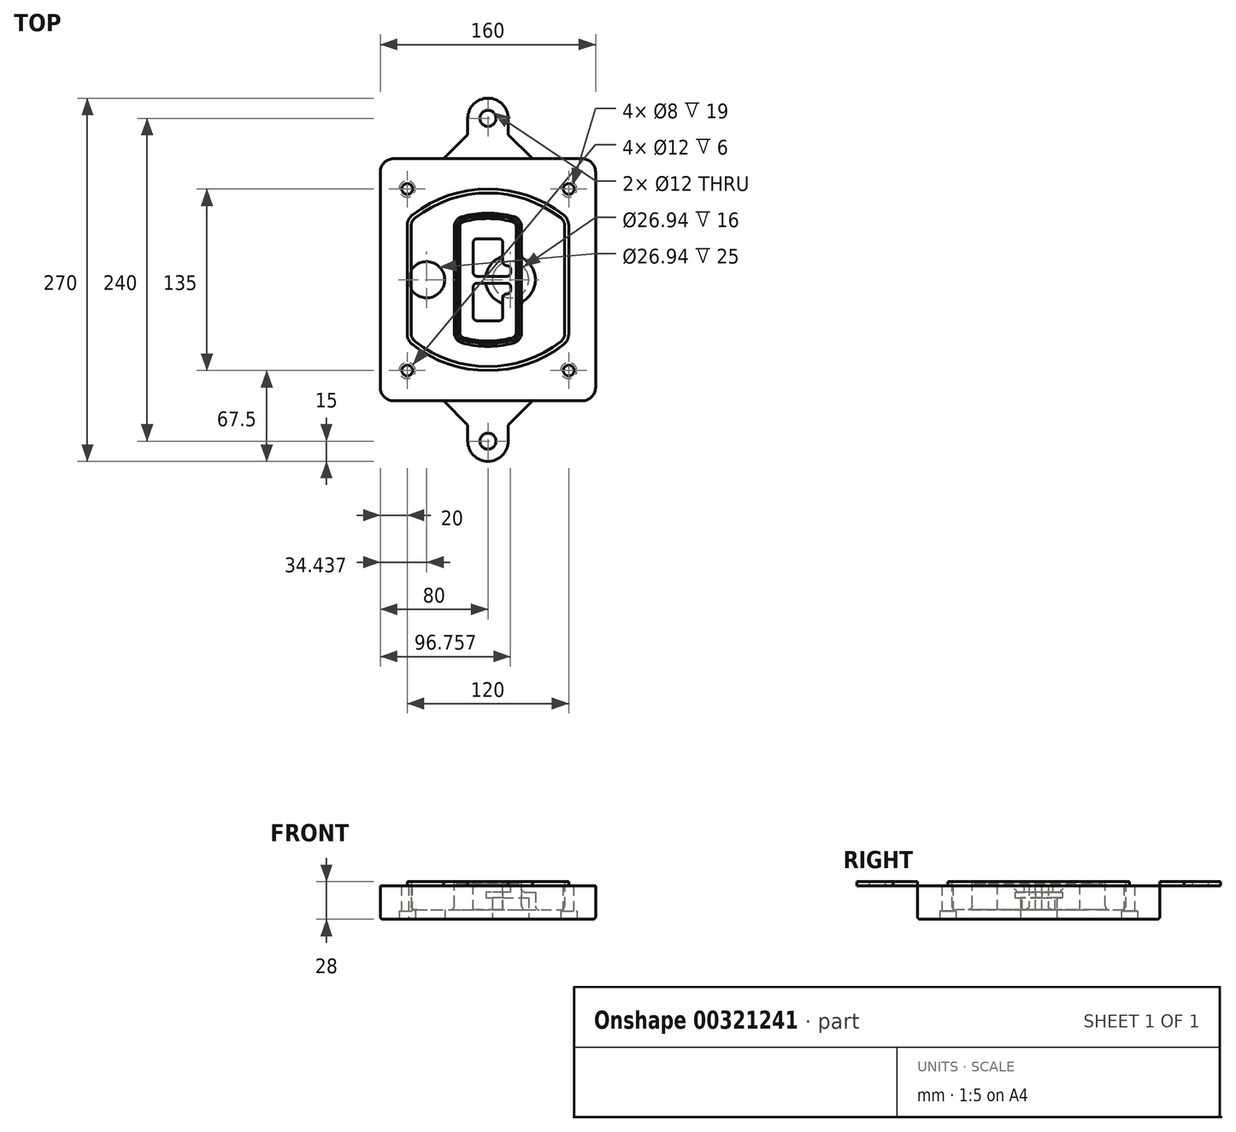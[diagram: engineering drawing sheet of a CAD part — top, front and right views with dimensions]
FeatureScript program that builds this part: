
annotation { "Feature Type Name" : "Feature", "Feature Type Description" : "" }
export const myFeature = defineFeature(function(context is Context, id is Id, definition is map)
    precondition{}
    {
        {
            var Q0;
            Q0=qCreatedBy(makeId("Top.planeOp"),FACE);
            var sketch = newSketch(context, id + "F0", { "sketchPlane" : qUnion([Q0])});
            skPoint(sketch, "E0.rect.middle", {"position": v(0, 0) * mm});
            skLineSegment(sketch, "E1.bottom", {"start": v(-70, -90) * mm, "end": v(70, -90) * mm});
            skLineSegment(sketch, "E1.top", {"start": v(-70, 90) * mm, "end": v(70, 90) * mm});
            skLineSegment(sketch, "E1.left", {"start": v(-80, -80) * mm, "end": v(-80, 80) * mm});
            skLineSegment(sketch, "E1.right", {"start": v(80, -80) * mm, "end": v(80, 80) * mm});
            skLineSegment(sketch, "E2", {"start": v(-80, 90) * mm, "end": v(80, -90) * mm, "construction": true});
            skLineSegment(sketch, "E3", {"start": v(80, 90) * mm, "end": v(-80, -90) * mm, "construction": true});
            skCircle(sketch, "E4", {"center": v(-60, 67.5) * mm, "radius": 4 * mm});
            skCircle(sketch, "E5", {"center": v(60, 67.5) * mm, "radius": 4 * mm});
            skCircle(sketch, "E6", {"center": v(60, -67.5) * mm, "radius": 4 * mm});
            skCircle(sketch, "E7", {"center": v(-60, -67.5) * mm, "radius": 4 * mm});
            skLineSegment(sketch, "E8", {"start": v(-60, 67.5) * mm, "end": v(60, 67.5) * mm, "construction": true});
            skLineSegment(sketch, "E9", {"start": v(60, 67.5) * mm, "end": v(60, -67.5) * mm, "construction": true});
            skLineSegment(sketch, "E10", {"start": v(60, -67.5) * mm, "end": v(-60, -67.5) * mm, "construction": true});
            skLineSegment(sketch, "E11", {"start": v(-60, -67.5) * mm, "end": v(-60, 67.5) * mm, "construction": true});
            skLineSegment(sketch, "E12", {"start": v(-60, 40.3) * mm, "end": v(-60, -40.3) * mm});
            skLineSegment(sketch, "E13", {"start": v(60, 40.3) * mm, "end": v(60, -40.3) * mm});
            skArc(sketch, "E14", {"start": v(56.15, 48.18) * mm, "mid": v(0, 67.5) * mm, "end": v(-56.15, 48.18) * mm});
            skArc(sketch, "E15", {"start": v(-56.15, -48.18) * mm, "mid": v(0, -67.5) * mm, "end": v(56.15, -48.18) * mm});
            skLineSegment(sketch, "E16", {"start": v(-60, 0) * mm, "end": v(60, 0) * mm, "construction": true});
            skPoint(sketch, "E17.visualSharp", {"position": v(-60, -45) * mm});
            skArc(sketch, "E17.filletArc", {"start": v(-60, -40.3) * mm, "mid": v(-58.99, -44.68) * mm, "end": v(-56.15, -48.18) * mm});
            skPoint(sketch, "E18.visualSharp", {"position": v(-60, 45) * mm});
            skArc(sketch, "E18.filletArc", {"start": v(-56.15, 48.18) * mm, "mid": v(-58.99, 44.68) * mm, "end": v(-60, 40.3) * mm});
            skPoint(sketch, "E19.visualSharp", {"position": v(60, 45) * mm});
            skArc(sketch, "E19.filletArc", {"start": v(60, 40.3) * mm, "mid": v(58.99, 44.68) * mm, "end": v(56.15, 48.18) * mm});
            skPoint(sketch, "E20.visualSharp", {"position": v(60, -45) * mm});
            skArc(sketch, "E20.filletArc", {"start": v(56.15, -48.18) * mm, "mid": v(58.99, -44.68) * mm, "end": v(60, -40.3) * mm});
            skPoint(sketch, "E21.visualSharp", {"position": v(-80, 90) * mm});
            skArc(sketch, "E21.filletArc", {"start": v(-70, 90) * mm, "mid": v(-77.07, 87.07) * mm, "end": v(-80, 80) * mm});
            skPoint(sketch, "E22.visualSharp", {"position": v(80, 90) * mm});
            skArc(sketch, "E22.filletArc", {"start": v(80, 80) * mm, "mid": v(77.07, 87.07) * mm, "end": v(70, 90) * mm});
            skPoint(sketch, "E23.visualSharp", {"position": v(80, -90) * mm});
            skArc(sketch, "E23.filletArc", {"start": v(70, -90) * mm, "mid": v(77.07, -87.07) * mm, "end": v(80, -80) * mm});
            skPoint(sketch, "E24.visualSharp", {"position": v(-80, -90) * mm});
            skArc(sketch, "E24.filletArc", {"start": v(-80, -80) * mm, "mid": v(-77.07, -87.07) * mm, "end": v(-70, -90) * mm});
            skArc(sketch, "E25.0", {"start": v(57, 40.3) * mm, "mid": v(56.3, 43.36) * mm, "end": v(54.3, 45.81) * mm});
            skLineSegment(sketch, "E25.1", {"start": v(57, 40.3) * mm, "end": v(57, -40.3) * mm});
            skArc(sketch, "E25.2", {"start": v(54.3, -45.81) * mm, "mid": v(56.3, -43.36) * mm, "end": v(57, -40.3) * mm});
            skArc(sketch, "E25.3", {"start": v(-54.3, -45.81) * mm, "mid": v(0, -64.5) * mm, "end": v(54.3, -45.81) * mm});
            skArc(sketch, "E25.4", {"start": v(-57, -40.3) * mm, "mid": v(-56.3, -43.36) * mm, "end": v(-54.3, -45.81) * mm});
            skArc(sketch, "E25.5", {"start": v(54.3, 45.81) * mm, "mid": v(0, 64.5) * mm, "end": v(-54.3, 45.81) * mm});
            skLineSegment(sketch, "E25.6", {"start": v(-57, 40.3) * mm, "end": v(-57, -40.3) * mm});
            skArc(sketch, "E25.7", {"start": v(-54.3, 45.81) * mm, "mid": v(-56.3, 43.36) * mm, "end": v(-57, 40.3) * mm});
            skArc(sketch, "E26.0", {"start": v(-58.62, 51.33) * mm, "mid": v(-62.58, 46.43) * mm, "end": v(-64, 40.3) * mm});
            skArc(sketch, "E26.1", {"start": v(58.62, 51.33) * mm, "mid": v(0, 71.5) * mm, "end": v(-58.62, 51.33) * mm});
            skArc(sketch, "E26.2", {"start": v(64, 40.3) * mm, "mid": v(62.58, 46.43) * mm, "end": v(58.62, 51.33) * mm});
            skLineSegment(sketch, "E26.3", {"start": v(64, 40.3) * mm, "end": v(64, -40.3) * mm});
            skArc(sketch, "E26.4", {"start": v(58.62, -51.33) * mm, "mid": v(62.58, -46.43) * mm, "end": v(64, -40.3) * mm});
            skLineSegment(sketch, "E26.5", {"start": v(-64, 40.3) * mm, "end": v(-64, -40.3) * mm});
            skArc(sketch, "E26.6", {"start": v(-58.62, -51.33) * mm, "mid": v(0, -71.5) * mm, "end": v(58.62, -51.33) * mm});
            skArc(sketch, "E26.7", {"start": v(-64, -40.3) * mm, "mid": v(-62.58, -46.43) * mm, "end": v(-58.62, -51.33) * mm});
            skSolve(sketch);
        }
        {
            var Q0;
            Q0=makeQuery(id+"F0.imprint","IMPRINT",FACE,{"disambiguationData":[TD([[makeQuery(id+"F0.imprint","IMPRINT",EDGE,{"derivedFrom":sQuery(id+"F0.wireOp",EDGE,"E1.bottom")}),1.0]])]});
            var Q1;
            Q1=makeQuery(id+"F0.imprint","IMPRINT",FACE,{"disambiguationData":[TD([[makeQuery(id+"F0.imprint","IMPRINT",EDGE,{"derivedFrom":sQuery(id+"F0.wireOp",EDGE,"E12")}),1.0]])]});
            var Q2;
            Q2=makeQuery(id+"F0.imprint","IMPRINT",FACE,{"disambiguationData":[TD([[makeQuery(id+"F0.imprint","IMPRINT",EDGE,{"derivedFrom":sQuery(id+"F0.wireOp",EDGE,"E25.0")}),1.0]])]});
            var Q3;
            Q3=makeQuery(id+"F0.imprint","IMPRINT",FACE,{"disambiguationData":[TD([[makeQuery(id+"F0.imprint","IMPRINT",EDGE,{"derivedFrom":sQuery(id+"F0.wireOp",EDGE,"E12")}),-1.0]])]});
            extrude(context, id + "F1", {"entities" : qUnion([Q0, Q1, Q2, Q3]), "oppositeDirection" : true, "depth" : 25 * mm});
        }
        {
            var Q0;
            Q0=makeQuery(id+"F0.imprint","IMPRINT",FACE,{"disambiguationData":[TD([[makeQuery(id+"F0.imprint","IMPRINT",EDGE,{"derivedFrom":sQuery(id+"F0.wireOp",EDGE,"E12")}),1.0]])]});
            extrude(context, id + "F2", {"entities" : qUnion([Q0]), "operationType" : NewBodyOperationType.ADD, "depth" : 3 * mm});
        }
        {
            var Q0;
            Q0=makeQuery(id+"F0.imprint","IMPRINT",FACE,{"disambiguationData":[TD([[makeQuery(id+"F0.imprint","IMPRINT",EDGE,{"derivedFrom":sQuery(id+"F0.wireOp",EDGE,"E25.0")}),1.0]])]});
            extrude(context, id + "F3", {"entities" : qUnion([Q0]), "operationType" : NewBodyOperationType.REMOVE, "oppositeDirection" : true, "depth" : 18 * mm});
        }
        {
            var Q0;
            Q0=makeQuery(id+"F2.opExtrude","CAP_FACE",FACE,{"disambiguationData":[OSD([sQuery(id+"F0.wireOp",EDGE,"E12"),sQuery(id+"F0.wireOp",EDGE,"E13"),sQuery(id+"F0.wireOp",EDGE,"E14"),sQuery(id+"F0.wireOp",EDGE,"E15"),sQuery(id+"F0.wireOp",EDGE,"E17.filletArc"),sQuery(id+"F0.wireOp",EDGE,"E18.filletArc"),sQuery(id+"F0.wireOp",EDGE,"E19.filletArc"),sQuery(id+"F0.wireOp",EDGE,"E20.filletArc"),sQuery(id+"F0.wireOp",EDGE,"E25.0"),sQuery(id+"F0.wireOp",EDGE,"E25.1"),sQuery(id+"F0.wireOp",EDGE,"E25.2"),sQuery(id+"F0.wireOp",EDGE,"E25.3"),sQuery(id+"F0.wireOp",EDGE,"E25.4"),sQuery(id+"F0.wireOp",EDGE,"E25.5"),sQuery(id+"F0.wireOp",EDGE,"E25.6"),sQuery(id+"F0.wireOp",EDGE,"E25.7")])],"isStart":false});
            var sketch = newSketch(context, id + "F4", { "sketchPlane" : qUnion([Q0])});
            skArc(sketch, "E27.0", {"start": v(-19.08, -46.97) * mm, "mid": v(0, -49.5) * mm, "end": v(19.08, -46.97) * mm});
            skArc(sketch, "E28.0", {"start": v(19.08, 46.97) * mm, "mid": v(0, 49.5) * mm, "end": v(-19.08, 46.97) * mm});
            skLineSegment(sketch, "E29", {"start": v(-25, 39.25) * mm, "end": v(-25, -39.25) * mm});
            skLineSegment(sketch, "E30", {"start": v(25, 39.25) * mm, "end": v(25, -39.25) * mm});
            skLineSegment(sketch, "E31", {"start": v(-25, 45.1) * mm, "end": v(25, 45.1) * mm, "construction": true});
            skLineSegment(sketch, "E32", {"start": v(-25, -45.1) * mm, "end": v(25, -45.1) * mm, "construction": true});
            skPoint(sketch, "E33.visualSharp", {"position": v(-25, 45.1) * mm});
            skArc(sketch, "E33.filletArc", {"start": v(-19.08, 46.97) * mm, "mid": v(-23.35, 44.11) * mm, "end": v(-25, 39.25) * mm});
            skPoint(sketch, "E34.visualSharp", {"position": v(25, 45.1) * mm});
            skArc(sketch, "E34.filletArc", {"start": v(25, 39.25) * mm, "mid": v(23.35, 44.11) * mm, "end": v(19.08, 46.97) * mm});
            skPoint(sketch, "E35.visualSharp", {"position": v(25, -45.1) * mm});
            skArc(sketch, "E35.filletArc", {"start": v(19.08, -46.97) * mm, "mid": v(23.35, -44.11) * mm, "end": v(25, -39.25) * mm});
            skPoint(sketch, "E36.visualSharp", {"position": v(-25, -45.1) * mm});
            skArc(sketch, "E36.filletArc", {"start": v(-25, -39.25) * mm, "mid": v(-23.35, -44.11) * mm, "end": v(-19.08, -46.97) * mm});
            skArc(sketch, "E37.0", {"start": v(54.3, 45.81) * mm, "mid": v(0, 64.5) * mm, "end": v(-54.3, 45.81) * mm});
            skArc(sketch, "E37.1", {"start": v(-54.3, 45.81) * mm, "mid": v(-56.3, 43.36) * mm, "end": v(-57, 40.3) * mm});
            skLineSegment(sketch, "E37.2", {"start": v(-57, 40.3) * mm, "end": v(-57, -40.3) * mm});
            skArc(sketch, "E37.3", {"start": v(-57, -40.3) * mm, "mid": v(-56.3, -43.36) * mm, "end": v(-54.3, -45.81) * mm});
            skArc(sketch, "E37.4", {"start": v(-54.3, -45.81) * mm, "mid": v(0, -64.5) * mm, "end": v(54.3, -45.81) * mm});
            skArc(sketch, "E37.5", {"start": v(54.3, -45.81) * mm, "mid": v(56.3, -43.36) * mm, "end": v(57, -40.3) * mm});
            skLineSegment(sketch, "E37.6", {"start": v(57, 40.3) * mm, "end": v(57, -40.3) * mm});
            skArc(sketch, "E37.7", {"start": v(57, 40.3) * mm, "mid": v(56.3, 43.36) * mm, "end": v(54.3, 45.81) * mm});
            skLineSegment(sketch, "E38.0", {"start": v(23, 39.25) * mm, "end": v(23, -39.25) * mm});
            skArc(sketch, "E38.1", {"start": v(18.56, -45.04) * mm, "mid": v(21.76, -42.9) * mm, "end": v(23, -39.25) * mm});
            skArc(sketch, "E38.2", {"start": v(-18.56, -45.04) * mm, "mid": v(0, -47.5) * mm, "end": v(18.56, -45.04) * mm});
            skArc(sketch, "E38.3", {"start": v(-23, -39.25) * mm, "mid": v(-21.76, -42.9) * mm, "end": v(-18.56, -45.04) * mm});
            skLineSegment(sketch, "E38.4", {"start": v(-23, 39.25) * mm, "end": v(-23, -39.25) * mm});
            skArc(sketch, "E38.5", {"start": v(23, 39.25) * mm, "mid": v(21.76, 42.9) * mm, "end": v(18.56, 45.04) * mm});
            skArc(sketch, "E38.6", {"start": v(-18.56, 45.04) * mm, "mid": v(-21.76, 42.9) * mm, "end": v(-23, 39.25) * mm});
            skArc(sketch, "E38.7", {"start": v(18.56, 45.04) * mm, "mid": v(0, 47.5) * mm, "end": v(-18.56, 45.04) * mm});
            skArc(sketch, "E39.0", {"start": v(21, 39.25) * mm, "mid": v(20.18, 41.68) * mm, "end": v(18.04, 43.1) * mm});
            skLineSegment(sketch, "E39.1", {"start": v(21, 39.25) * mm, "end": v(21, -39.25) * mm});
            skArc(sketch, "E39.2", {"start": v(18.04, -43.1) * mm, "mid": v(20.18, -41.68) * mm, "end": v(21, -39.25) * mm});
            skArc(sketch, "E39.3", {"start": v(-18.04, -43.1) * mm, "mid": v(0, -45.5) * mm, "end": v(18.04, -43.1) * mm});
            skArc(sketch, "E39.4", {"start": v(-21, -39.25) * mm, "mid": v(-20.18, -41.68) * mm, "end": v(-18.04, -43.1) * mm});
            skArc(sketch, "E39.5", {"start": v(18.04, 43.1) * mm, "mid": v(0, 45.5) * mm, "end": v(-18.04, 43.1) * mm});
            skLineSegment(sketch, "E39.6", {"start": v(-21, 39.25) * mm, "end": v(-21, -39.25) * mm});
            skArc(sketch, "E39.7", {"start": v(-18.04, 43.1) * mm, "mid": v(-20.18, 41.68) * mm, "end": v(-21, 39.25) * mm});
            skLineSegment(sketch, "E40", {"start": v(-25, 0) * mm, "end": v(25, 0) * mm, "construction": true});
            skLineSegment(sketch, "E41", {"start": v(-11, 5.5) * mm, "end": v(-11, 27.5) * mm});
            skLineSegment(sketch, "E42", {"start": v(-8, 30.5) * mm, "end": v(8, 30.5) * mm});
            skLineSegment(sketch, "E43", {"start": v(11, 27.5) * mm, "end": v(11, 13.5) * mm});
            skLineSegment(sketch, "E44", {"start": v(14, 10.5) * mm, "end": v(14, 10.5) * mm});
            skLineSegment(sketch, "E45", {"start": v(17, 7.5) * mm, "end": v(17, 5.5) * mm});
            skLineSegment(sketch, "E46", {"start": v(14, 2.5) * mm, "end": v(-8, 2.5) * mm});
            skPoint(sketch, "E47.visualSharp", {"position": v(-11, 30.5) * mm});
            skArc(sketch, "E47.filletArc", {"start": v(-8, 30.5) * mm, "mid": v(-10.12, 29.62) * mm, "end": v(-11, 27.5) * mm});
            skPoint(sketch, "E48.visualSharp", {"position": v(11, 30.5) * mm});
            skArc(sketch, "E48.filletArc", {"start": v(11, 27.5) * mm, "mid": v(10.12, 29.62) * mm, "end": v(8, 30.5) * mm});
            skPoint(sketch, "E49.visualSharp", {"position": v(11, 10.5) * mm});
            skArc(sketch, "E49.filletArc", {"start": v(11, 13.5) * mm, "mid": v(11.88, 11.38) * mm, "end": v(14, 10.5) * mm});
            skPoint(sketch, "E50.visualSharp", {"position": v(17, 10.5) * mm});
            skArc(sketch, "E50.filletArc", {"start": v(17, 7.5) * mm, "mid": v(16.12, 9.62) * mm, "end": v(14, 10.5) * mm});
            skPoint(sketch, "E51.visualSharp", {"position": v(17, 2.5) * mm});
            skArc(sketch, "E51.filletArc", {"start": v(14, 2.5) * mm, "mid": v(16.12, 3.38) * mm, "end": v(17, 5.5) * mm});
            skPoint(sketch, "E52.visualSharp", {"position": v(-11, 2.5) * mm});
            skArc(sketch, "E52.filletArc", {"start": v(-11, 5.5) * mm, "mid": v(-10.12, 3.38) * mm, "end": v(-8, 2.5) * mm});
            skLineSegment(sketch, "E53.0.MirrorCS", {"start": v(14, -2.5) * mm, "end": v(-8, -2.5) * mm});
            skArc(sketch, "E54.0.MirrorCS", {"start": v(-11, -5.5) * mm, "mid": v(-10.12, -3.38) * mm, "end": v(-8, -2.5) * mm});
            skLineSegment(sketch, "E55.0.MirrorCS", {"start": v(-11, -5.5) * mm, "end": v(-11, -27.5) * mm});
            skArc(sketch, "E56.0.MirrorCS", {"start": v(-8, -30.5) * mm, "mid": v(-10.12, -29.62) * mm, "end": v(-11, -27.5) * mm});
            skLineSegment(sketch, "E57.0.MirrorCS", {"start": v(-8, -30.5) * mm, "end": v(8, -30.5) * mm});
            skArc(sketch, "E58.0.MirrorCS", {"start": v(11, -27.5) * mm, "mid": v(10.12, -29.62) * mm, "end": v(8, -30.5) * mm});
            skLineSegment(sketch, "E59.0.MirrorCS", {"start": v(11, -27.5) * mm, "end": v(11, -13.5) * mm});
            skArc(sketch, "E60.0.MirrorCS", {"start": v(11, -13.5) * mm, "mid": v(11.88, -11.38) * mm, "end": v(14, -10.5) * mm});
            skArc(sketch, "E61.0.MirrorCS", {"start": v(17, -7.5) * mm, "mid": v(16.12, -9.62) * mm, "end": v(14, -10.5) * mm});
            skLineSegment(sketch, "E62.0.MirrorCS", {"start": v(17, -7.5) * mm, "end": v(17, -5.5) * mm});
            skArc(sketch, "E63.0.MirrorCS", {"start": v(14, -2.5) * mm, "mid": v(16.12, -3.38) * mm, "end": v(17, -5.5) * mm});
            skSolve(sketch);
        }
        {
            var Q0;
            Q0=makeQuery(id+"F4.imprint","IMPRINT",FACE,{"disambiguationData":[TD([[makeQuery(id+"F4.imprint","IMPRINT",EDGE,{"derivedFrom":sQuery(id+"F4.wireOp",EDGE,"E27.0")}),1.0]])]});
            var Q1;
            Q1=makeQuery(id+"F4.imprint","IMPRINT",FACE,{"disambiguationData":[TD([[makeQuery(id+"F4.imprint","IMPRINT",EDGE,{"derivedFrom":sQuery(id+"F4.wireOp",EDGE,"E38.0")}),-1.0]])]});
            var Q2;
            Q2=makeQuery(id+"F4.imprint","IMPRINT",FACE,{"disambiguationData":[TD([[makeQuery(id+"F4.imprint","IMPRINT",EDGE,{"derivedFrom":sQuery(id+"F4.wireOp",EDGE,"E39.0")}),1.0]])]});
            extrude(context, id + "F5", {"entities" : qUnion([Q0, Q1, Q2]), "operationType" : NewBodyOperationType.ADD, "endBound" : BoundingType.UP_TO_NEXT, "oppositeDirection" : true, "depth" : 25 * mm});
        }
        {
            var Q0;
            Q0=makeQuery(id+"F4.imprint","IMPRINT",FACE,{"disambiguationData":[TD([[makeQuery(id+"F4.imprint","IMPRINT",EDGE,{"derivedFrom":sQuery(id+"F4.wireOp",EDGE,"E38.0")}),-1.0]])]});
            extrude(context, id + "F6", {"entities" : qUnion([Q0]), "operationType" : NewBodyOperationType.REMOVE, "oppositeDirection" : true, "depth" : 2 * mm});
        }
        {
            var Q0;
            Q0=makeQuery(id+"F1.opExtrude","CAP_FACE",FACE,{"disambiguationData":[OSD([sQuery(id+"F0.wireOp",EDGE,"E1.bottom"),sQuery(id+"F0.wireOp",EDGE,"E1.top"),sQuery(id+"F0.wireOp",EDGE,"E1.left"),sQuery(id+"F0.wireOp",EDGE,"E1.right"),sQuery(id+"F0.wireOp",EDGE,"E4"),sQuery(id+"F0.wireOp",EDGE,"E5"),sQuery(id+"F0.wireOp",EDGE,"E6"),sQuery(id+"F0.wireOp",EDGE,"E7"),sQuery(id+"F0.wireOp",EDGE,"E21.filletArc"),sQuery(id+"F0.wireOp",EDGE,"E22.filletArc"),sQuery(id+"F0.wireOp",EDGE,"E23.filletArc"),sQuery(id+"F0.wireOp",EDGE,"E24.filletArc")])],"isStart":false});
            var sketch = newSketch(context, id + "F7", { "sketchPlane" : qUnion([Q0])});
            skCircle(sketch, "E64", {"center": v(16.76, 0) * mm, "radius": 13.47 * mm});
            skCircle(sketch, "E65", {"center": v(-45.56, 0) * mm, "radius": 13.47 * mm});
            skLineSegment(sketch, "E66", {"start": v(80, 0) * mm, "end": v(-80, 0) * mm});
            skCircle(sketch, "E67", {"center": v(16.76, 0) * mm, "radius": 18.47 * mm});
            skCircle(sketch, "E68", {"center": v(60, -67.5) * mm, "radius": 6 * mm});
            skCircle(sketch, "E69", {"center": v(-60, -67.5) * mm, "radius": 6 * mm});
            skCircle(sketch, "E70", {"center": v(-60, 67.5) * mm, "radius": 6 * mm});
            skCircle(sketch, "E71", {"center": v(60, 67.5) * mm, "radius": 6 * mm});
            skSolve(sketch);
        }
        {
            var Q0;
            {var subQ1=sQuery(id+"F7.wireOp",EDGE,"E66");var subQ4=sQuery(id+"F7.wireOp",EDGE,"E64");var subQ6=makeQuery(id+"F7.imprint","INTERSECT",VERTEX,{"disambiguationData":[OD(0.0)],"derivedFrom":[subQ4,subQ1]});Q0=makeQuery(id+"F7.imprint","IMPRINT",FACE,{"disambiguationData":[TD([[makeQuery(id+"F7.imprint","IMPRINT",EDGE,{"disambiguationData":[TD([[subQ6,-1.0]])],"derivedFrom":subQ4}),-1.0]])]});}
            var Q1;
            {var subQ0=sQuery(id+"F7.wireOp",EDGE,"E66");var subQ1=sQuery(id+"F7.wireOp",EDGE,"E64");var subQ3=makeQuery(id+"F7.imprint","INTERSECT",VERTEX,{"disambiguationData":[OD(0.0)],"derivedFrom":[subQ1,subQ0]});Q1=makeQuery(id+"F7.imprint","IMPRINT",FACE,{"disambiguationData":[TD([[makeQuery(id+"F7.imprint","IMPRINT",EDGE,{"disambiguationData":[TD([[subQ3,-1.0]])],"derivedFrom":subQ1}),1.0]])]});}
            var Q2;
            {var subQ0=sQuery(id+"F7.wireOp",EDGE,"E66");var subQ1=sQuery(id+"F7.wireOp",EDGE,"E64");var subQ3=makeQuery(id+"F7.imprint","INTERSECT",VERTEX,{"disambiguationData":[OD(0.0)],"derivedFrom":[subQ1,subQ0]});Q2=makeQuery(id+"F7.imprint","IMPRINT",FACE,{"disambiguationData":[TD([[makeQuery(id+"F7.imprint","IMPRINT",EDGE,{"disambiguationData":[TD([[subQ3,1.0]])],"derivedFrom":subQ1}),1.0]])]});}
            var Q3;
            {var subQ1=sQuery(id+"F7.wireOp",EDGE,"E66");var subQ4=sQuery(id+"F7.wireOp",EDGE,"E64");var subQ6=makeQuery(id+"F7.imprint","INTERSECT",VERTEX,{"disambiguationData":[OD(0.0)],"derivedFrom":[subQ4,subQ1]});Q3=makeQuery(id+"F7.imprint","IMPRINT",FACE,{"disambiguationData":[TD([[makeQuery(id+"F7.imprint","IMPRINT",EDGE,{"disambiguationData":[TD([[subQ6,1.0]])],"derivedFrom":subQ4}),-1.0]])]});}
            extrude(context, id + "F8", {"entities" : qUnion([Q0, Q1, Q2, Q3]), "operationType" : NewBodyOperationType.ADD, "oppositeDirection" : true, "depth" : 20 * mm});
        }
        {
            var Q0;
            {var subQ0=sQuery(id+"F7.wireOp",EDGE,"E66");var subQ1=sQuery(id+"F7.wireOp",EDGE,"E64");var subQ3=makeQuery(id+"F7.imprint","INTERSECT",VERTEX,{"disambiguationData":[OD(0.0)],"derivedFrom":[subQ1,subQ0]});Q0=makeQuery(id+"F7.imprint","IMPRINT",FACE,{"disambiguationData":[TD([[makeQuery(id+"F7.imprint","IMPRINT",EDGE,{"disambiguationData":[TD([[subQ3,-1.0]])],"derivedFrom":subQ1}),1.0]])]});}
            var Q1;
            {var subQ0=sQuery(id+"F7.wireOp",EDGE,"E66");var subQ1=sQuery(id+"F7.wireOp",EDGE,"E64");var subQ3=makeQuery(id+"F7.imprint","INTERSECT",VERTEX,{"disambiguationData":[OD(0.0)],"derivedFrom":[subQ1,subQ0]});Q1=makeQuery(id+"F7.imprint","IMPRINT",FACE,{"disambiguationData":[TD([[makeQuery(id+"F7.imprint","IMPRINT",EDGE,{"disambiguationData":[TD([[subQ3,1.0]])],"derivedFrom":subQ1}),1.0]])]});}
            extrude(context, id + "F9", {"entities" : qUnion([Q0, Q1]), "operationType" : NewBodyOperationType.REMOVE, "oppositeDirection" : true, "depth" : 16 * mm});
        }
        {
            var Q0;
            {var subQ0=sQuery(id+"F7.wireOp",EDGE,"E66");var subQ1=sQuery(id+"F7.wireOp",EDGE,"E65");var subQ3=makeQuery(id+"F7.imprint","INTERSECT",VERTEX,{"disambiguationData":[OD(0.0)],"derivedFrom":[subQ1,subQ0]});Q0=makeQuery(id+"F7.imprint","IMPRINT",FACE,{"disambiguationData":[TD([[makeQuery(id+"F7.imprint","IMPRINT",EDGE,{"disambiguationData":[TD([[subQ3,-1.0]])],"derivedFrom":subQ1}),1.0]])]});}
            var Q1;
            {var subQ0=sQuery(id+"F7.wireOp",EDGE,"E66");var subQ1=sQuery(id+"F7.wireOp",EDGE,"E65");var subQ3=makeQuery(id+"F7.imprint","INTERSECT",VERTEX,{"disambiguationData":[OD(0.0)],"derivedFrom":[subQ1,subQ0]});Q1=makeQuery(id+"F7.imprint","IMPRINT",FACE,{"disambiguationData":[TD([[makeQuery(id+"F7.imprint","IMPRINT",EDGE,{"disambiguationData":[TD([[subQ3,1.0]])],"derivedFrom":subQ1}),1.0]])]});}
            extrude(context, id + "F10", {"entities" : qUnion([Q0, Q1]), "operationType" : NewBodyOperationType.REMOVE, "oppositeDirection" : true, "depth" : 25 * mm});
        }
        {
            var Q0;
            Q0=makeQuery(id+"F7.imprint","IMPRINT",FACE,{"disambiguationData":[TD([[makeQuery(id+"F7.imprint","IMPRINT",EDGE,{"derivedFrom":sQuery(id+"F7.wireOp",EDGE,"E68")}),1.0]])]});
            var Q1;
            Q1=makeQuery(id+"F7.imprint","IMPRINT",FACE,{"disambiguationData":[TD([[makeQuery(id+"F7.imprint","IMPRINT",EDGE,{"derivedFrom":makeQuery(id+"F1.opExtrude","CAP_EDGE",EDGE,{"disambiguationData":[OSD([sQuery(id+"F0.wireOp",EDGE,"E5")])],"isStart":false})}),-1.0]])]});
            var Q2;
            Q2=makeQuery(id+"F7.imprint","IMPRINT",FACE,{"disambiguationData":[TD([[makeQuery(id+"F7.imprint","IMPRINT",EDGE,{"derivedFrom":sQuery(id+"F7.wireOp",EDGE,"E69")}),1.0]])]});
            var Q3;
            Q3=makeQuery(id+"F7.imprint","IMPRINT",FACE,{"disambiguationData":[TD([[makeQuery(id+"F7.imprint","IMPRINT",EDGE,{"derivedFrom":makeQuery(id+"F1.opExtrude","CAP_EDGE",EDGE,{"disambiguationData":[OSD([sQuery(id+"F0.wireOp",EDGE,"E4")])],"isStart":false})}),-1.0]])]});
            var Q4;
            Q4=makeQuery(id+"F7.imprint","IMPRINT",FACE,{"disambiguationData":[TD([[makeQuery(id+"F7.imprint","IMPRINT",EDGE,{"derivedFrom":sQuery(id+"F7.wireOp",EDGE,"E70")}),1.0]])]});
            var Q5;
            Q5=makeQuery(id+"F7.imprint","IMPRINT",FACE,{"disambiguationData":[TD([[makeQuery(id+"F7.imprint","IMPRINT",EDGE,{"derivedFrom":makeQuery(id+"F1.opExtrude","CAP_EDGE",EDGE,{"disambiguationData":[OSD([sQuery(id+"F0.wireOp",EDGE,"E7")])],"isStart":false})}),-1.0]])]});
            var Q6;
            Q6=makeQuery(id+"F7.imprint","IMPRINT",FACE,{"disambiguationData":[TD([[makeQuery(id+"F7.imprint","IMPRINT",EDGE,{"derivedFrom":sQuery(id+"F7.wireOp",EDGE,"E71")}),1.0]])]});
            var Q7;
            Q7=makeQuery(id+"F7.imprint","IMPRINT",FACE,{"disambiguationData":[TD([[makeQuery(id+"F7.imprint","IMPRINT",EDGE,{"derivedFrom":makeQuery(id+"F1.opExtrude","CAP_EDGE",EDGE,{"disambiguationData":[OSD([sQuery(id+"F0.wireOp",EDGE,"E6")])],"isStart":false})}),-1.0]])]});
            extrude(context, id + "F11", {"entities" : qUnion([Q0, Q1, Q2, Q3, Q4, Q5, Q6, Q7]), "operationType" : NewBodyOperationType.REMOVE, "oppositeDirection" : true, "depth" : 6 * mm});
        }
        {
            var Q0;
            Q0=makeQuery(id+"F9.boolean.opBoolean","COPY",FACE,{"derivedFrom":makeQuery(id+"F9.opExtrude","CAP_FACE",FACE,{"disambiguationData":[OSD([sQuery(id+"F7.wireOp",EDGE,"E64")])],"isStart":false})});
            var sketch = newSketch(context, id + "F12", { "sketchPlane" : qUnion([Q0])});
            skArc(sketch, "E72.0", {"start": v(11, 17.55) * mm, "mid": v(2.57, 11.82) * mm, "end": v(-1.54, 2.5) * mm});
            skArc(sketch, "E72.1", {"start": v(-1.54, -2.5) * mm, "mid": v(2.57, -11.82) * mm, "end": v(11, -17.55) * mm});
            skLineSegment(sketch, "E73", {"start": v(-1.54, -2.5) * mm, "end": v(14, -2.5) * mm});
            skLineSegment(sketch, "E74.0", {"start": v(14, 2.5) * mm, "end": v(-1.54, 2.5) * mm});
            skArc(sketch, "E74.1", {"start": v(14, 2.5) * mm, "mid": v(16.12, 3.38) * mm, "end": v(17, 5.5) * mm});
            skLineSegment(sketch, "E74.2", {"start": v(17, 7.5) * mm, "end": v(17, 5.5) * mm});
            skArc(sketch, "E74.3", {"start": v(17, 7.5) * mm, "mid": v(16.12, 9.62) * mm, "end": v(14, 10.5) * mm});
            skArc(sketch, "E74.4", {"start": v(11, 13.5) * mm, "mid": v(11.88, 11.38) * mm, "end": v(14, 10.5) * mm});
            skLineSegment(sketch, "E74.5", {"start": v(11, 17.55) * mm, "end": v(11, 13.5) * mm});
            skLineSegment(sketch, "E74.7", {"start": v(14, -2.5) * mm, "end": v(-1.54, -2.5) * mm});
            skArc(sketch, "E74.8", {"start": v(14, -2.5) * mm, "mid": v(16.12, -3.38) * mm, "end": v(17, -5.5) * mm});
            skLineSegment(sketch, "E74.9", {"start": v(17, -7.5) * mm, "end": v(17, -5.5) * mm});
            skArc(sketch, "E74.10", {"start": v(17, -7.5) * mm, "mid": v(16.12, -9.62) * mm, "end": v(14, -10.5) * mm});
            skArc(sketch, "E74.11", {"start": v(11, -13.5) * mm, "mid": v(11.88, -11.38) * mm, "end": v(14, -10.5) * mm});
            skLineSegment(sketch, "E74.12", {"start": v(11, -17.55) * mm, "end": v(11, -13.5) * mm});
            skPoint(sketch, "E75.orphan", {"position": v(11, -27.5) * mm});
            skPoint(sketch, "E76.orphan", {"position": v(-8, -2.5) * mm});
            skPoint(sketch, "E77.orphan", {"position": v(-8, 2.5) * mm});
            skPoint(sketch, "E78.orphan", {"position": v(11, 27.5) * mm});
            skSolve(sketch);
        }
        {
            var Q0;
            {var subQ7=sQuery(id+"F12.wireOp",EDGE,"E72.0");var subQ14=sQuery(id+"F12.wireOp",EDGE,"E72.1");var subQ16=sQuery(id+"F12.wireOp",EDGE,"E74.1");var subQ18=sQuery(id+"F12.wireOp",EDGE,"E74.8");Q0=qUnion([makeQuery(id+"F12.imprint","IMPRINT",FACE,{"disambiguationData":[TD([[makeQuery(id+"F12.imprint","IMPRINT",EDGE,{"derivedFrom":subQ7}),1.0]])]}),makeQuery(id+"F12.imprint","IMPRINT",FACE,{"disambiguationData":[TD([[makeQuery(id+"F12.imprint","IMPRINT",EDGE,{"derivedFrom":subQ14}),1.0]])]}),makeQuery(id+"F12.imprint","IMPRINT",FACE,{"disambiguationData":[TD([[makeQuery(id+"F12.imprint","IMPRINT",EDGE,{"derivedFrom":subQ16}),1.0]])]}),makeQuery(id+"F12.imprint","IMPRINT",FACE,{"disambiguationData":[TD([[makeQuery(id+"F12.imprint","IMPRINT",EDGE,{"derivedFrom":subQ18}),-1.0]])]})]);}
            var Q1;
            Q1=makeQuery(id+"F5.boolean.opBoolean","SPLIT",FACE,{"disambiguationData":[TD([makeQuery(id+"F5.opExtrude","SWEPT_FACE",FACE,{"disambiguationData":[OSD([sQuery(id+"F4.wireOp",EDGE,"E41")])]})])],"derivedFrom":makeQuery(id+"F3.boolean.opBoolean","COPY",FACE,{"derivedFrom":makeQuery(id+"F3.opExtrude","CAP_FACE",FACE,{"disambiguationData":[OSD([sQuery(id+"F0.wireOp",EDGE,"E25.0"),sQuery(id+"F0.wireOp",EDGE,"E25.1"),sQuery(id+"F0.wireOp",EDGE,"E25.2"),sQuery(id+"F0.wireOp",EDGE,"E25.3"),sQuery(id+"F0.wireOp",EDGE,"E25.4"),sQuery(id+"F0.wireOp",EDGE,"E25.5"),sQuery(id+"F0.wireOp",EDGE,"E25.6"),sQuery(id+"F0.wireOp",EDGE,"E25.7")])],"isStart":false})})});
            extrude(context, id + "F13", {"entities" : qUnion([Q0]), "operationType" : NewBodyOperationType.REMOVE, "endBound" : BoundingType.UP_TO_SURFACE, "endBoundEntityFace" : qUnion([Q1]), "depth" : 25 * mm});
        }
        {
            var Q0;
            Q0=makeQuery(id+"F3.boolean.opBoolean","COPY",EDGE,{"derivedFrom":makeQuery(id+"F3.opExtrude","CAP_EDGE",EDGE,{"disambiguationData":[OSD([sQuery(id+"F0.wireOp",EDGE,"E25.6")])],"isStart":false})});
            var Q1;
            Q1=makeQuery(id+"F8.boolean.opBoolean","INTERSECT",EDGE,{"derivedFrom":[makeQuery(id+"F5.opExtrude","SWEPT_FACE",FACE,{"disambiguationData":[OSD([sQuery(id+"F4.wireOp",EDGE,"E30")])]}),makeQuery(id+"F8.opExtrude","CAP_FACE",FACE,{"disambiguationData":[OSD([sQuery(id+"F7.wireOp",EDGE,"E67")])],"isStart":false})]});
            var Q2;
            Q2=makeQuery(id+"F8.boolean.opBoolean","INTERSECT",EDGE,{"disambiguationData":[OD(1.0)],"derivedFrom":[makeQuery(id+"F5.opExtrude","SWEPT_FACE",FACE,{"disambiguationData":[OSD([sQuery(id+"F4.wireOp",EDGE,"E30")])]}),makeQuery(id+"F8.opExtrude","SWEPT_FACE",FACE,{"disambiguationData":[OSD([sQuery(id+"F7.wireOp",EDGE,"E67")])]})]});
            var Q3;
            {var subQ0=sQuery(id+"F4.wireOp",EDGE,"E30");Q3=makeQuery(id+"F8.boolean.opBoolean","SPLIT",EDGE,{"disambiguationData":[TD([makeQuery(id+"F5.opExtrude","SWEPT_FACE",FACE,{"disambiguationData":[OSD([sQuery(id+"F4.wireOp",EDGE,"E35.filletArc")])]})])],"derivedFrom":makeQuery(id+"F5.opExtrude","CAP_EDGE",EDGE,{"disambiguationData":[OSD([subQ0])],"isStart":false})});}
            var Q4;
            {var subQ0=sQuery(id+"F0.wireOp",EDGE,"E25.7");var subQ1=sQuery(id+"F0.wireOp",EDGE,"E25.1");var subQ2=sQuery(id+"F0.wireOp",EDGE,"E25.6");var subQ3=sQuery(id+"F0.wireOp",EDGE,"E25.5");var subQ4=sQuery(id+"F0.wireOp",EDGE,"E25.4");var subQ5=sQuery(id+"F0.wireOp",EDGE,"E25.0");var subQ6=sQuery(id+"F0.wireOp",EDGE,"E25.2");var subQ7=sQuery(id+"F0.wireOp",EDGE,"E25.3");Q4=makeQuery(id+"F8.boolean.opBoolean","INTERSECT",EDGE,{"derivedFrom":[makeQuery(id+"F5.boolean.opBoolean","SPLIT",FACE,{"disambiguationData":[TD([makeQuery(id+"F2.opExtrude","SWEPT_FACE",FACE,{"disambiguationData":[OSD([subQ5])]})])],"derivedFrom":makeQuery(id+"F3.boolean.opBoolean","COPY",FACE,{"derivedFrom":makeQuery(id+"F3.opExtrude","CAP_FACE",FACE,{"disambiguationData":[OSD([subQ5,subQ1,subQ6,subQ7,subQ4,subQ3,subQ2,subQ0])],"isStart":false})})}),makeQuery(id+"F8.opExtrude","SWEPT_FACE",FACE,{"disambiguationData":[OSD([sQuery(id+"F7.wireOp",EDGE,"E67")])]})]});}
            var Q5;
            Q5=makeQuery(id+"F8.boolean.opBoolean","INTERSECT",EDGE,{"disambiguationData":[OD(0.0)],"derivedFrom":[makeQuery(id+"F5.opExtrude","SWEPT_FACE",FACE,{"disambiguationData":[OSD([sQuery(id+"F4.wireOp",EDGE,"E30")])]}),makeQuery(id+"F8.opExtrude","SWEPT_FACE",FACE,{"disambiguationData":[OSD([sQuery(id+"F7.wireOp",EDGE,"E67")])]})]});
            fillet(context, id + "F14", {"entities" : qUnion([Q0, Q1, Q2, Q3, Q4, Q5]), "radius" : 3 * mm, "tangentPropagation" : true, "allowEdgeOverflow" : false});
        }
        {
            var Q0;
            Q0=makeQuery(id+"F1.opExtrude","CAP_EDGE",EDGE,{"disambiguationData":[OSD([sQuery(id+"F0.wireOp",EDGE,"E1.bottom")])],"isStart":false});
            fillet(context, id + "F15", {"entities" : qUnion([Q0]), "radius" : 2 * mm, "tangentPropagation" : true, "allowEdgeOverflow" : false});
        }
        {
            var Q0;
            Q0=qCreatedBy(makeId("Top.planeOp"),FACE);
            var sketch = newSketch(context, id + "F16", { "sketchPlane" : qUnion([Q0])});
            skLineSegment(sketch, "E79.0", {"start": v(-80, -80) * mm, "end": v(-80, 80) * mm});
            skArc(sketch, "E79.1", {"start": v(-70, 90) * mm, "mid": v(-77.07, 87.07) * mm, "end": v(-80, 80) * mm});
            skLineSegment(sketch, "E79.2", {"start": v(-70, 90) * mm, "end": v(70, 90) * mm});
            skArc(sketch, "E79.3", {"start": v(-80, -80) * mm, "mid": v(-77.07, -87.07) * mm, "end": v(-70, -90) * mm});
            skLineSegment(sketch, "E79.4", {"start": v(-70, -90) * mm, "end": v(70, -90) * mm});
            skArc(sketch, "E79.5", {"start": v(70, -90) * mm, "mid": v(77.07, -87.07) * mm, "end": v(80, -80) * mm});
            skLineSegment(sketch, "E79.6", {"start": v(80, -80) * mm, "end": v(80, 80) * mm});
            skArc(sketch, "E79.7", {"start": v(80, 80) * mm, "mid": v(77.07, 87.07) * mm, "end": v(70, 90) * mm});
            skCircle(sketch, "E79.8", {"center": v(60, 67.5) * mm, "radius": 4 * mm});
            skCircle(sketch, "E79.9", {"center": v(-60, -67.5) * mm, "radius": 4 * mm});
            skCircle(sketch, "E79.10", {"center": v(60, -67.5) * mm, "radius": 4 * mm});
            skCircle(sketch, "E79.11", {"center": v(-60, 67.5) * mm, "radius": 4 * mm});
            skLineSegment(sketch, "E80", {"start": v(0, 90) * mm, "end": v(0, 120) * mm, "construction": true});
            skPoint(sketch, "E81", {"position": v(0, 90) * mm});
            skLineSegment(sketch, "E82", {"start": v(-33, 90) * mm, "end": v(-15, 108) * mm});
            skLineSegment(sketch, "E83", {"start": v(-15, 108) * mm, "end": v(-15, 120) * mm});
            skLineSegment(sketch, "E84", {"start": v(15, 108) * mm, "end": v(33, 90) * mm});
            skLineSegment(sketch, "E85", {"start": v(33, 90) * mm, "end": v(15, 108) * mm});
            skLineSegment(sketch, "E86", {"start": v(15, 120) * mm, "end": v(15, 108) * mm});
            skArc(sketch, "E87", {"start": v(15, 120) * mm, "mid": v(0, 135) * mm, "end": v(-15, 120) * mm});
            skCircle(sketch, "E88", {"center": v(0, 120) * mm, "radius": 6 * mm});
            skLineSegment(sketch, "E89", {"start": v(-80, 0) * mm, "end": v(0, 0) * mm, "construction": true});
            skLineSegment(sketch, "E90", {"start": v(0, 0) * mm, "end": v(80, 0) * mm, "construction": true});
            skLineSegment(sketch, "E91.MirrorCS", {"start": v(15, -108) * mm, "end": v(33, -90) * mm});
            skLineSegment(sketch, "E92.MirrorCS", {"start": v(-33, -90) * mm, "end": v(-15, -108) * mm});
            skLineSegment(sketch, "E93.MirrorCS", {"start": v(-15, -108) * mm, "end": v(-15, -120) * mm});
            skLineSegment(sketch, "E94.MirrorCS", {"start": v(15, -120) * mm, "end": v(15, -108) * mm});
            skArc(sketch, "E95.MirrorCS", {"start": v(15, -120) * mm, "mid": v(0, -135) * mm, "end": v(-15, -120) * mm});
            skCircle(sketch, "E96.MirrorC", {"center": v(0, -120) * mm, "radius": 6 * mm});
            skSolve(sketch);
        }
        {
            var Q0;
            {var subQ0=sQuery(id+"F16.wireOp",EDGE,"E82");Q0=makeQuery(id+"F16.imprint","IMPRINT",FACE,{"disambiguationData":[TD([[makeQuery(id+"F16.imprint","IMPRINT",EDGE,{"derivedFrom":subQ0}),-1.0]])]});}
            var Q1;
            {var subQ1=sQuery(id+"F16.wireOp",EDGE,"E91.MirrorCS");Q1=makeQuery(id+"F16.imprint","IMPRINT",FACE,{"disambiguationData":[TD([[makeQuery(id+"F16.imprint","IMPRINT",EDGE,{"derivedFrom":subQ1}),1.0]])]});}
            var Q2;
            Q2=makeQuery(id+"F2.opExtrude","CAP_FACE",FACE,{"disambiguationData":[OSD([sQuery(id+"F0.wireOp",EDGE,"E12"),sQuery(id+"F0.wireOp",EDGE,"E13"),sQuery(id+"F0.wireOp",EDGE,"E14"),sQuery(id+"F0.wireOp",EDGE,"E15"),sQuery(id+"F0.wireOp",EDGE,"E17.filletArc"),sQuery(id+"F0.wireOp",EDGE,"E18.filletArc"),sQuery(id+"F0.wireOp",EDGE,"E19.filletArc"),sQuery(id+"F0.wireOp",EDGE,"E20.filletArc"),sQuery(id+"F0.wireOp",EDGE,"E25.0"),sQuery(id+"F0.wireOp",EDGE,"E25.1"),sQuery(id+"F0.wireOp",EDGE,"E25.2"),sQuery(id+"F0.wireOp",EDGE,"E25.3"),sQuery(id+"F0.wireOp",EDGE,"E25.4"),sQuery(id+"F0.wireOp",EDGE,"E25.5"),sQuery(id+"F0.wireOp",EDGE,"E25.6"),sQuery(id+"F0.wireOp",EDGE,"E25.7")])],"isStart":false});
            extrude(context, id + "F17", {"entities" : qUnion([Q0, Q1]), "endBound" : BoundingType.UP_TO_SURFACE, "endBoundEntityFace" : qUnion([Q2]), "depth" : 25 * mm});
        }
    });
